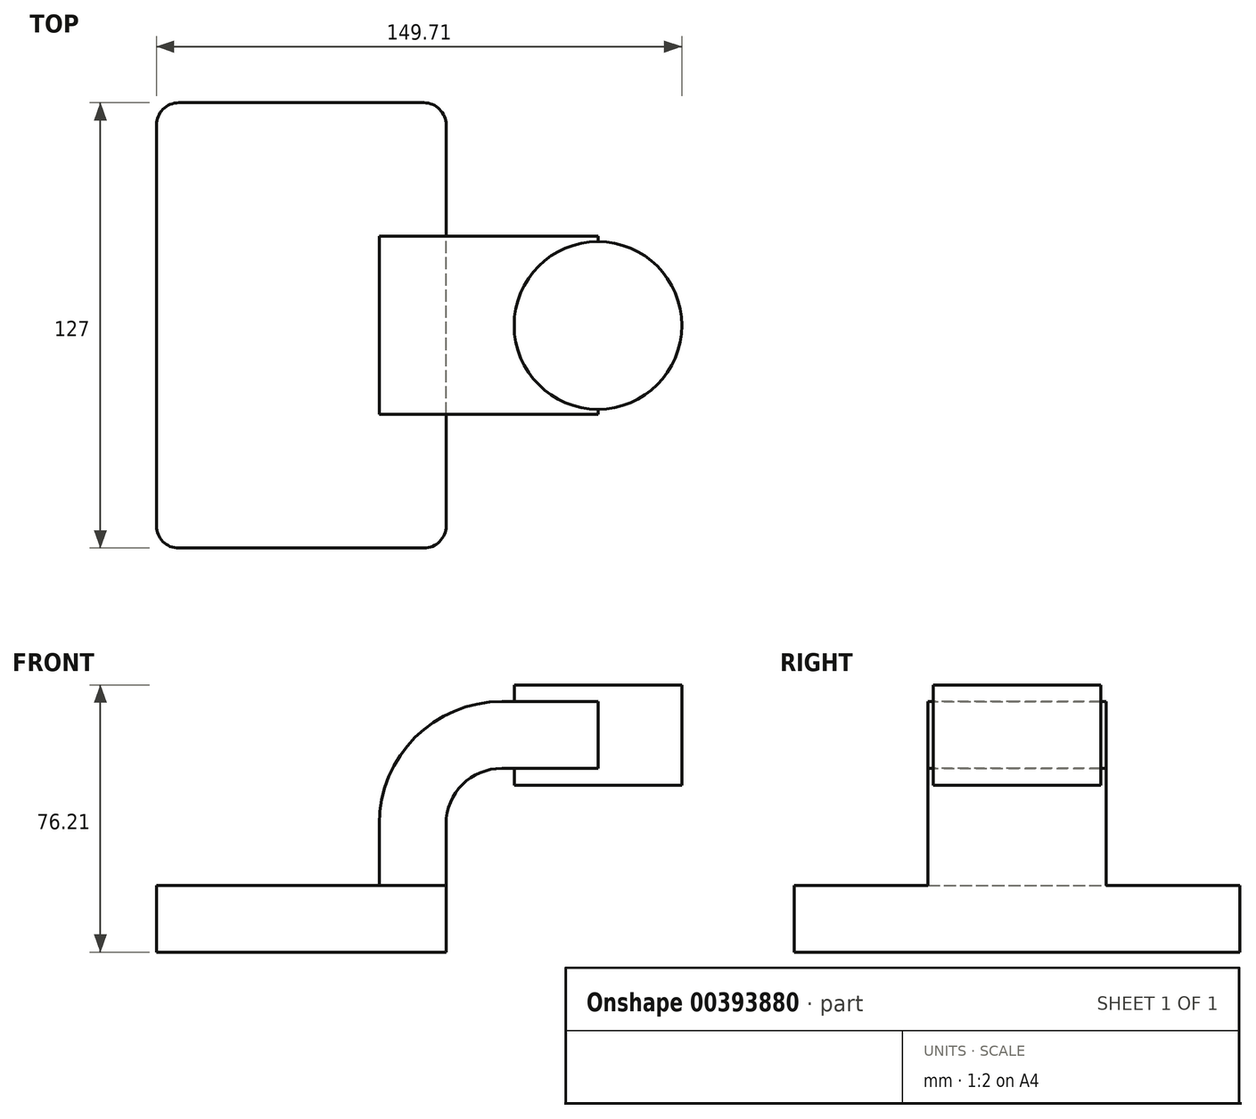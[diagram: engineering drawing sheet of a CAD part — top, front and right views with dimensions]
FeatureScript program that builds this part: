
annotation { "Feature Type Name" : "Feature", "Feature Type Description" : "" }
export const myFeature = defineFeature(function(context is Context, id is Id, definition is map)
    precondition{}
    {
        {
            var Q0;
            Q0=qCreatedBy(makeId("Front.planeOp"),FACE);
            var sketch = newSketch(context, id + "F0", { "sketchPlane" : qUnion([Q0])});
            skLineSegment(sketch, "E0.bottom", {"start": v(41.28, -9.52) * mm, "end": v(-41.28, -9.53) * mm});
            skLineSegment(sketch, "E0.top", {"start": v(41.28, 9.53) * mm, "end": v(-41.28, 9.53) * mm});
            skLineSegment(sketch, "E0.left", {"start": v(41.28, -9.52) * mm, "end": v(41.28, 9.53) * mm});
            skLineSegment(sketch, "E0.right", {"start": v(-41.28, -9.53) * mm, "end": v(-41.28, 9.53) * mm});
            skPoint(sketch, "E0.middle", {"position": v(0, 0) * mm});
            skLineSegment(sketch, "E1.bottom", {"start": v(108.44, 38.1) * mm, "end": v(57.64, 38.1) * mm});
            skLineSegment(sketch, "E1.top", {"start": v(108.44, 66.68) * mm, "end": v(57.64, 66.68) * mm});
            skLineSegment(sketch, "E1.left", {"start": v(108.44, 38.1) * mm, "end": v(108.44, 66.68) * mm});
            skLineSegment(sketch, "E1.right", {"start": v(57.64, 38.1) * mm, "end": v(57.64, 66.68) * mm});
            skPoint(sketch, "E1.middle", {"position": v(83.04, 52.39) * mm});
            skLineSegment(sketch, "E2", {"start": v(41.28, 9.53) * mm, "end": v(41.28, 27) * mm});
            skArc(sketch, "E3", {"start": v(41.27, 27) * mm, "mid": v(45.92, 38.23) * mm, "end": v(57.15, 42.88) * mm});
            skLineSegment(sketch, "E4", {"start": v(57.15, 42.88) * mm, "end": v(84.55, 42.88) * mm});
            skLineSegment(sketch, "E5.0", {"start": v(57.15, 61.93) * mm, "end": v(84.55, 61.93) * mm});
            skArc(sketch, "E5.1", {"start": v(22.23, 27) * mm, "mid": v(32.45, 51.7) * mm, "end": v(57.15, 61.93) * mm});
            skLineSegment(sketch, "E5.2", {"start": v(22.22, 9.53) * mm, "end": v(22.22, 27) * mm});
            skLineSegment(sketch, "E6", {"start": v(84.55, 42.88) * mm, "end": v(84.55, 61.93) * mm});
            skFitSpline(sketch, "E7", {"points": [v(-41.28, 9.52) * mm, v(57.15, 61.93) * mm], "startDerivative": vector(-1.08, 56.66) * mm, "endDerivative": vector(123.35, -3.83) * mm});
            skLineSegment(sketch, "E8", {"start": v(84.55, 42.88) * mm, "end": v(84.55, 38.1) * mm});
            skPoint(sketch, "E8.endSnap0", {"position": v(83.04, 38.1) * mm});
            skLineSegment(sketch, "E9", {"start": v(84.55, 61.93) * mm, "end": v(84.55, 66.68) * mm});
            skSolve(sketch);
        }
        {
            var Q0;
            Q0=makeQuery(id+"F0.imprint","IMPRINT",FACE,{"disambiguationData":[TD([[makeQuery(id+"F0.imprint","IMPRINT",EDGE,{"derivedFrom":sQuery(id+"F0.wireOp",EDGE,"E0.bottom")}),-1.0]])]});
            extrude(context, id + "F1", {"entities" : qUnion([Q0]), "endBound" : BoundingType.SYMMETRIC, "depth" : 127 * mm});
        }
        {
            var Q0;
            {var subQ1=sQuery(id+"F0.wireOp",EDGE,"E2");Q0=makeQuery(id+"F0.imprint","IMPRINT",FACE,{"disambiguationData":[TD([[makeQuery(id+"F0.imprint","IMPRINT",EDGE,{"derivedFrom":subQ1}),1.0]])]});}
            var Q1;
            {var subQ5=sQuery(id+"F0.wireOp",EDGE,"E6");Q1=makeQuery(id+"F0.imprint","IMPRINT",FACE,{"disambiguationData":[TD([[makeQuery(id+"F0.imprint","IMPRINT",EDGE,{"derivedFrom":subQ5}),1.0]])]});}
            extrude(context, id + "F2", {"entities" : qUnion([Q0, Q1]), "operationType" : NewBodyOperationType.ADD, "endBound" : BoundingType.SYMMETRIC, "depth" : 50.8 * mm});
        }
        {
            var Q0;
            Q0=makeQuery(id+"F0.imprint","IMPRINT",FACE,{"disambiguationData":[TD([[makeQuery(id+"F0.imprint","IMPRINT",EDGE,{"derivedFrom":sQuery(id+"F0.wireOp",EDGE,"E5.1")}),1.0]])]});
            extrude(context, id + "F3", {"entities" : qUnion([Q0]), "operationType" : NewBodyOperationType.ADD, "endBound" : BoundingType.SYMMETRIC, "depth" : 15.88 * mm});
        }
        {
            var Q0;
            {var subQ0=sQuery(id+"F0.wireOp",EDGE,"E1.left");Q0=makeQuery(id+"F0.imprint","IMPRINT",FACE,{"disambiguationData":[TD([[makeQuery(id+"F0.imprint","IMPRINT",EDGE,{"derivedFrom":subQ0}),1.0]])]});}
            var Q1;
            Q1=sQuery(id+"F0.wireOp",EDGE,"E6");
            revolve(context, id + "F4", {"operationType" : NewBodyOperationType.ADD, "entities" : qUnion([Q0]), "axis" : qUnion([Q1]), "revolveType" : RevolveType.FULL});
        }
        {
            var Q0;
            Q0=makeQuery(id+"F1.opExtrude","CAP_EDGE",EDGE,{"disambiguationData":[OSD([sQuery(id+"F0.wireOp",EDGE,"E0.left")])],"isStart":false});
            var Q1;
            Q1=makeQuery(id+"F1.opExtrude","CAP_EDGE",EDGE,{"disambiguationData":[OSD([sQuery(id+"F0.wireOp",EDGE,"E0.right")])],"isStart":false});
            var Q2;
            Q2=makeQuery(id+"F1.opExtrude","CAP_EDGE",EDGE,{"disambiguationData":[OSD([sQuery(id+"F0.wireOp",EDGE,"E0.left")])],"isStart":true});
            var Q3;
            Q3=makeQuery(id+"F1.opExtrude","CAP_EDGE",EDGE,{"disambiguationData":[OSD([sQuery(id+"F0.wireOp",EDGE,"E0.right")])],"isStart":true});
            fillet(context, id + "F5", {"entities" : qUnion([Q0, Q1, Q2, Q3]), "radius" : 6.35 * mm, "tangentPropagation" : true, "allowEdgeOverflow" : false});
        }
    });
